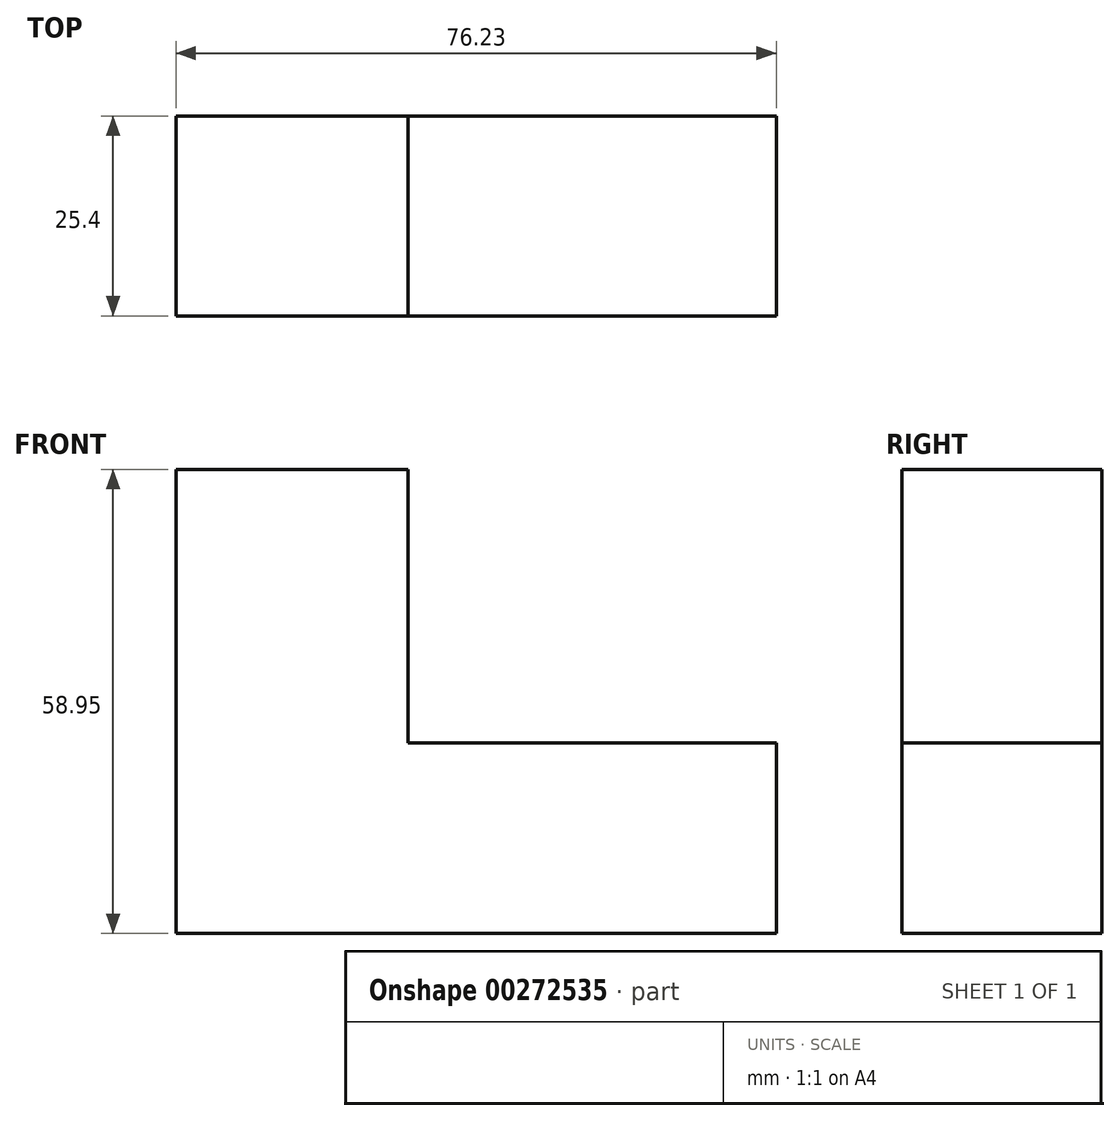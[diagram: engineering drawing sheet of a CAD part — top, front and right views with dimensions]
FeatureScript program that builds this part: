
annotation { "Feature Type Name" : "Feature", "Feature Type Description" : "" }
export const myFeature = defineFeature(function(context is Context, id is Id, definition is map)
    precondition{}
    {
        {
            var Q0;
            Q0=qCreatedBy(makeId("Front.planeOp"),FACE);
            var sketch = newSketch(context, id + "F0", { "sketchPlane" : qUnion([Q0])});
            skLineSegment(sketch, "E0", {"start": v(0, 0) * mm, "end": v(-76.23, 0) * mm});
            skLineSegment(sketch, "E1", {"start": v(-76.23, 0) * mm, "end": v(-76.23, 58.95) * mm});
            skLineSegment(sketch, "E2", {"start": v(-76.23, 58.95) * mm, "end": v(-46.78, 58.95) * mm});
            skLineSegment(sketch, "E3", {"start": v(-46.78, 58.95) * mm, "end": v(-46.78, 24.19) * mm});
            skLineSegment(sketch, "E4", {"start": v(-46.78, 24.19) * mm, "end": v(0, 24.19) * mm});
            skLineSegment(sketch, "E5", {"start": v(0, 0) * mm, "end": v(0, 24.19) * mm});
            skSolve(sketch);
        }
        {
            var Q0;
            Q0=makeQuery(id+"F0.imprint","IMPRINT",FACE,{"disambiguationData":[TD([[makeQuery(id+"F0.imprint","IMPRINT",EDGE,{"derivedFrom":sQuery(id+"F0.wireOp",EDGE,"E0")}),-1.0]])]});
            extrude(context, id + "F1", {"entities" : qUnion([Q0]), "depth" : 25.4 * mm});
        }
    });
